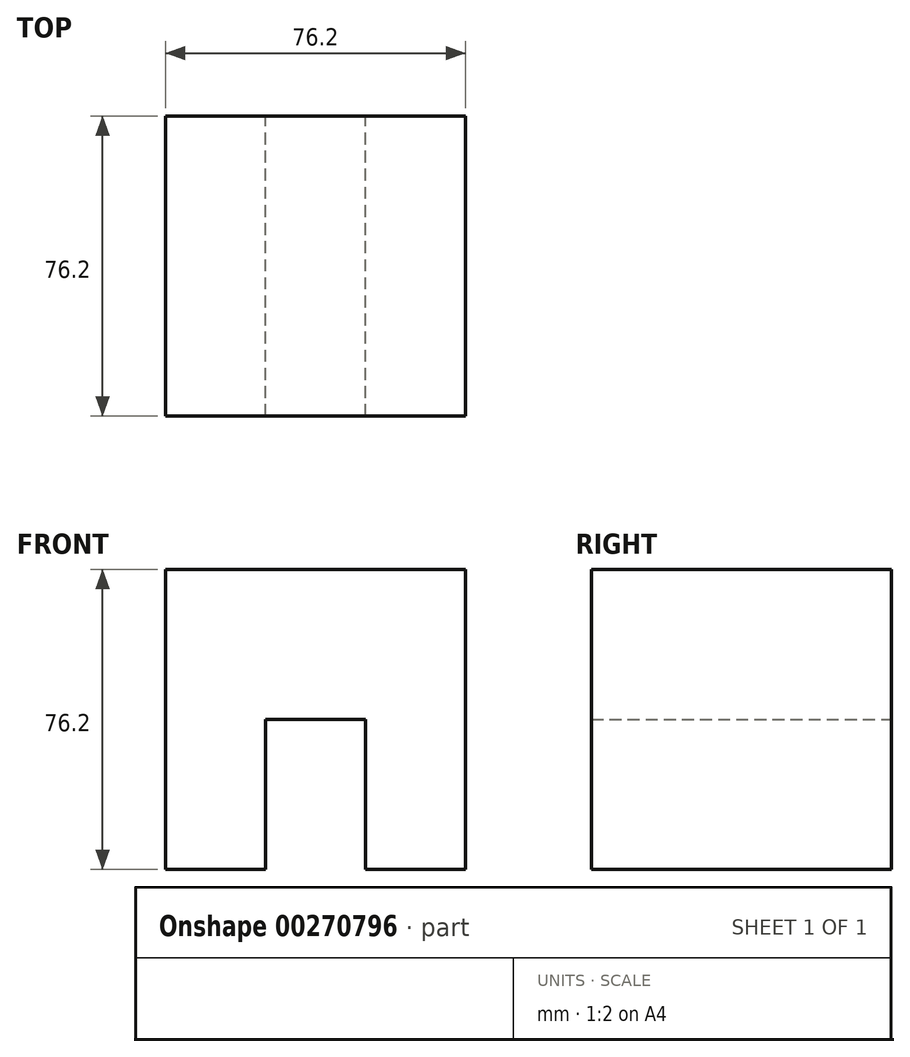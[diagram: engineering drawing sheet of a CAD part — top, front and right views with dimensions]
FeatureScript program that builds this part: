
annotation { "Feature Type Name" : "Feature", "Feature Type Description" : "" }
export const myFeature = defineFeature(function(context is Context, id is Id, definition is map)
    precondition{}
    {
        {
            var Q0;
            Q0=qCreatedBy(makeId("Front.planeOp"),FACE);
            var sketch = newSketch(context, id + "F0", { "sketchPlane" : qUnion([Q0])});
            skLineSegment(sketch, "E0", {"start": v(-39.45, 43.2) * mm, "end": v(36.75, 43.2) * mm});
            skLineSegment(sketch, "E1", {"start": v(36.75, 43.2) * mm, "end": v(36.75, -33) * mm});
            skLineSegment(sketch, "E2", {"start": v(36.75, -33) * mm, "end": v(11.35, -33) * mm});
            skLineSegment(sketch, "E3", {"start": v(11.35, -33) * mm, "end": v(11.35, 5.1) * mm});
            skLineSegment(sketch, "E4", {"start": v(11.35, 5.1) * mm, "end": v(-14.05, 5.1) * mm});
            skLineSegment(sketch, "E5", {"start": v(-14.05, 5.1) * mm, "end": v(-14.05, -33) * mm});
            skLineSegment(sketch, "E6", {"start": v(-14.05, -33) * mm, "end": v(-39.45, -33) * mm});
            skLineSegment(sketch, "E7", {"start": v(-39.45, -33) * mm, "end": v(-39.45, 43.2) * mm});
            skSolve(sketch);
        }
        {
            var Q0;
            Q0 = qSketchRegion(id + "F0", true);
            extrude(context, id + "F1", {"entities" : qUnion([Q0]), "depth" : 76.2 * mm});
        }
    });
